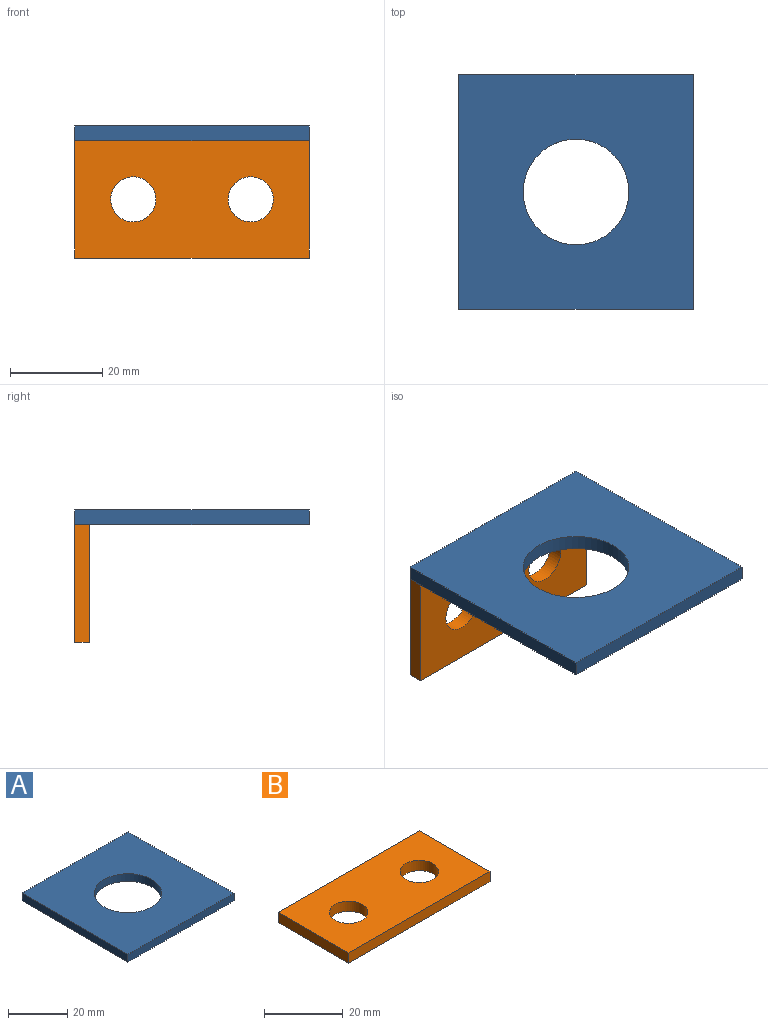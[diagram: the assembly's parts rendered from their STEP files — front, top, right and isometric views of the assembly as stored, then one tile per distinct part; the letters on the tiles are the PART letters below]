
ASSEMBLY  parts=2 mates=1
PART A: 7 faces, bbox 50.8x50.8x3.2 mm
  f0: plane 50.8x3.18mm, normal (0,1,0), area 161.3mm2, adj f1,f4,f5,f6
  f1: plane 50.8x3.18mm, normal (-1,0,0), area 161.3mm2, adj f0,f2,f5,f6
  f2: plane 50.8x3.18mm, normal (0,-1,0), area 161.3mm2, adj f1,f4,f5,f6
  f3: cylinder r=11.43mm len=22.86mm, axis (0,0,-1), area 228mm2, adj f5,f6
  f4: plane 50.8x3.18mm, normal (1,0,0), area 161.3mm2, adj f0,f2,f5,f6
  f5: plane 50.8x50.8mm, normal (0,0,1), area 2170.2mm2, adj f0,f1,f2,f3,f4
  f6: plane 50.8x50.8mm, normal (0,0,-1), area 2170.2mm2, adj f0,f1,f2,f3,f4
PART B: 8 faces, bbox 50.8x25.4x3.2 mm
  f0: plane 50.8x3.18mm, normal (0,1,0), area 161.3mm2, adj f1,f5,f6,f7
  f1: plane 25.4x3.18mm, normal (-1,0,0), area 80.6mm2, adj f0,f2,f6,f7
  f2: plane 50.8x3.18mm, normal (0,-1,0), area 161.3mm2, adj f1,f5,f6,f7
  f3: cylinder r=4.88mm len=9.77mm, axis (0,0,-1), area 97.4mm2, adj f6,f7
  f4: cylinder r=4.88mm len=9.77mm, axis (0,0,-1), area 97.4mm2, adj f6,f7
  f5: plane 25.4x3.18mm, normal (1,0,0), area 80.6mm2, adj f0,f2,f6,f7
  f6: plane 50.8x25.4mm, normal (0,0,1), area 1140.4mm2, adj f0,f1,f2,f3,f4,f5
  f7: plane 50.8x25.4mm, normal (0,0,-1), area 1140.4mm2, adj f0,f1,f2,f3,f4,f5
PLACE A t=(-15.99,-14.59,-9.63)mm
PLACE B rot(axis=(-1,0,0),90deg) t=(-15.99,7.63,-22.33)mm
MATE fastened B.f2 <-> A.f6  axis (0,0,1) through (-15.99,10.81,-9.63)mm
